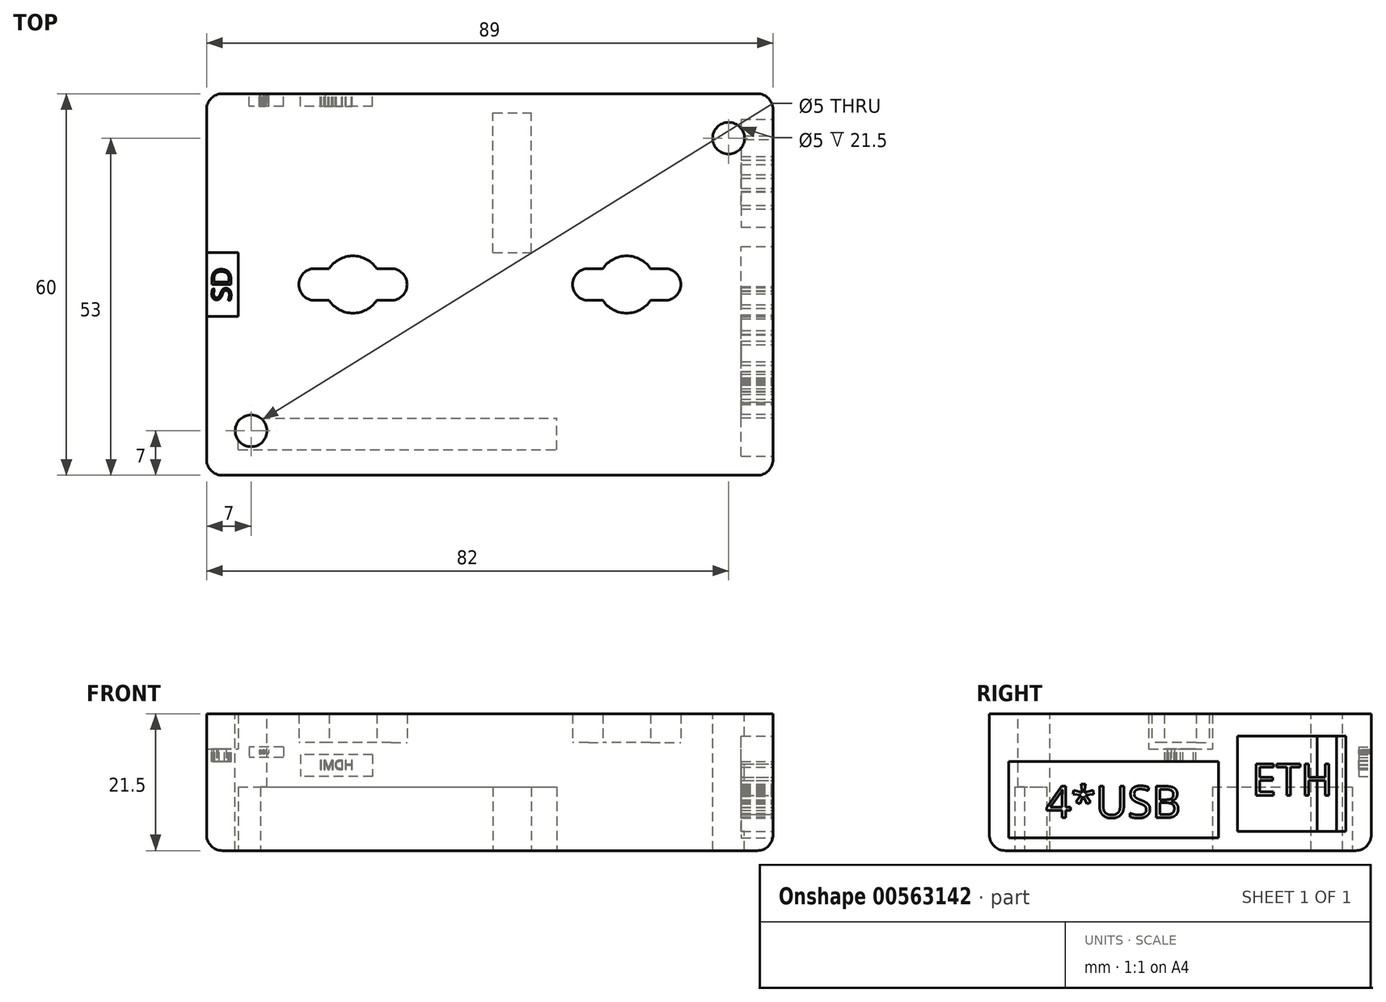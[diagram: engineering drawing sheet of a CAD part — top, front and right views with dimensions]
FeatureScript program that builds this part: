
annotation { "Feature Type Name" : "Feature", "Feature Type Description" : "" }
export const myFeature = defineFeature(function(context is Context, id is Id, definition is map)
    precondition{}
    {
        {
            var Q0;
            Q0=qCreatedBy(makeId("Top.planeOp"),FACE);
            var sketch = newSketch(context, id + "F0", { "sketchPlane" : qUnion([Q0])});
            skLineSegment(sketch, "E0.bottom", {"start": v(44.5, -30) * mm, "end": v(-44.5, -30) * mm});
            skLineSegment(sketch, "E0.top", {"start": v(44.5, 30) * mm, "end": v(-44.5, 30) * mm});
            skLineSegment(sketch, "E0.left", {"start": v(44.5, -30) * mm, "end": v(44.5, 30) * mm});
            skLineSegment(sketch, "E0.right", {"start": v(-44.5, -30) * mm, "end": v(-44.5, 30) * mm});
            skPoint(sketch, "E0.middle", {"position": v(0, 0) * mm});
            skLineSegment(sketch, "E1", {"start": v(-44.5, 0) * mm, "end": v(44.5, 0) * mm, "construction": true});
            skCircle(sketch, "E2", {"center": v(-37.5, 23) * mm, "radius": 2.5 * mm});
            skLineSegment(sketch, "E3", {"start": v(-37.5, 23) * mm, "end": v(-44.5, 23) * mm, "construction": true});
            skLineSegment(sketch, "E4", {"start": v(-44.5, 23) * mm, "end": v(-37.5, 23) * mm, "construction": true});
            skLineSegment(sketch, "E5", {"start": v(-37.5, 23) * mm, "end": v(-37.5, 30) * mm, "construction": true});
            skCircle(sketch, "E6", {"center": v(0, 0) * mm, "radius": 3.04 * mm, "construction": true});
            skCircle(sketch, "E7.MirrorC", {"center": v(-37.5, -23) * mm, "radius": 2.5 * mm});
            skLineSegment(sketch, "E8", {"start": v(0, 0) * mm, "end": v(0, 30) * mm, "construction": true});
            skCircle(sketch, "E9.MirrorC", {"center": v(37.5, 23) * mm, "radius": 2.5 * mm});
            skCircle(sketch, "E10.MirrorC", {"center": v(37.5, -23) * mm, "radius": 2.5 * mm});
            skArc(sketch, "E11", {"start": v(17.76, -2.5) * mm, "mid": v(21.5, -4.5) * mm, "end": v(25.24, -2.5) * mm});
            skArc(sketch, "E12", {"start": v(15.5, 2.5) * mm, "mid": v(13, 0) * mm, "end": v(15.5, -2.5) * mm});
            skLineSegment(sketch, "E13", {"start": v(15.5, 0) * mm, "end": v(21.5, 0) * mm, "construction": true});
            skLineSegment(sketch, "E14", {"start": v(21.5, 0) * mm, "end": v(44.5, 0) * mm, "construction": true});
            skLineSegment(sketch, "E15", {"start": v(21.5, 0) * mm, "end": v(21.5, 12.26) * mm, "construction": true});
            skArc(sketch, "E16.MirrorC", {"start": v(27.5, 2.5) * mm, "mid": v(30, 0) * mm, "end": v(27.5, -2.5) * mm});
            skLineSegment(sketch, "E17", {"start": v(15.5, 2.5) * mm, "end": v(17.76, 2.5) * mm});
            skLineSegment(sketch, "E18.MirrorCS", {"start": v(15.5, -2.5) * mm, "end": v(17.76, -2.5) * mm});
            skLineSegment(sketch, "E19.trimOffspring", {"start": v(25.24, 2.5) * mm, "end": v(27.5, 2.5) * mm});
            skArc(sketch, "E20.trimOffspring", {"start": v(25.24, 2.5) * mm, "mid": v(21.5, 4.5) * mm, "end": v(17.76, 2.5) * mm});
            skLineSegment(sketch, "E21.trimOffspring", {"start": v(25.24, -2.5) * mm, "end": v(27.5, -2.5) * mm});
            skLineSegment(sketch, "E22.MirrorCS", {"start": v(-15.5, -2.5) * mm, "end": v(-17.76, -2.5) * mm});
            skLineSegment(sketch, "E23.MirrorCS", {"start": v(-25.24, -2.5) * mm, "end": v(-27.5, -2.5) * mm});
            skLineSegment(sketch, "E24.MirrorCS", {"start": v(-25.24, 2.5) * mm, "end": v(-27.5, 2.5) * mm});
            skLineSegment(sketch, "E25.MirrorCS", {"start": v(-15.5, 2.5) * mm, "end": v(-17.76, 2.5) * mm});
            skArc(sketch, "E26.MirrorCS", {"start": v(-15.5, 2.5) * mm, "mid": v(-13, 0) * mm, "end": v(-15.5, -2.5) * mm});
            skArc(sketch, "E27.MirrorCS", {"start": v(-27.5, 2.5) * mm, "mid": v(-30, 0) * mm, "end": v(-27.5, -2.5) * mm});
            skLineSegment(sketch, "E28.MirrorCS", {"start": v(-15.5, 0) * mm, "end": v(-21.5, 0) * mm, "construction": true});
            skArc(sketch, "E29.MirrorCS", {"start": v(-25.24, 2.5) * mm, "mid": v(-21.5, 4.5) * mm, "end": v(-17.76, 2.5) * mm});
            skArc(sketch, "E30.MirrorCS", {"start": v(-17.76, -2.5) * mm, "mid": v(-21.5, -4.5) * mm, "end": v(-25.24, -2.5) * mm});
            skLineSegment(sketch, "E31.bottom", {"start": v(-44.5, -5) * mm, "end": v(-39.5, -5) * mm});
            skLineSegment(sketch, "E31.top", {"start": v(-44.5, 5) * mm, "end": v(-39.5, 5) * mm});
            skLineSegment(sketch, "E31.left", {"start": v(-44.5, -5) * mm, "end": v(-44.5, 5) * mm});
            skLineSegment(sketch, "E31.right", {"start": v(-39.5, -5) * mm, "end": v(-39.5, 5) * mm});
            skPoint(sketch, "E32", {"position": v(-39.5, 0) * mm});
            skSolve(sketch);
        }
        {
            var Q0;
            Q0=makeQuery(id+"F0.imprint","IMPRINT",FACE,{"disambiguationData":[TD([[makeQuery(id+"F0.imprint","IMPRINT",EDGE,{"derivedFrom":sQuery(id+"F0.wireOp",EDGE,"E0.bottom")}),-1.0]])]});
            var Q1;
            Q1=makeQuery(id+"F0.imprint","IMPRINT",FACE,{"disambiguationData":[TD([[makeQuery(id+"F0.imprint","IMPRINT",EDGE,{"derivedFrom":sQuery(id+"F0.wireOp",EDGE,"E7.MirrorC")}),-1.0]])]});
            var Q2;
            Q2=makeQuery(id+"F0.imprint","IMPRINT",FACE,{"disambiguationData":[TD([[makeQuery(id+"F0.imprint","IMPRINT",EDGE,{"derivedFrom":sQuery(id+"F0.wireOp",EDGE,"E10.MirrorC")}),1.0]])]});
            var Q3;
            Q3=makeQuery(id+"F0.imprint","IMPRINT",FACE,{"disambiguationData":[TD([[makeQuery(id+"F0.imprint","IMPRINT",EDGE,{"derivedFrom":sQuery(id+"F0.wireOp",EDGE,"E9.MirrorC")}),-1.0]])]});
            var Q4;
            Q4=makeQuery(id+"F0.imprint","IMPRINT",FACE,{"disambiguationData":[TD([[makeQuery(id+"F0.imprint","IMPRINT",EDGE,{"derivedFrom":sQuery(id+"F0.wireOp",EDGE,"E2")}),1.0]])]});
            var Q5;
            {var subQ0=sQuery(id+"F0.wireOp",EDGE,"E12");var subQ1=sQuery(id+"F0.wireOp",EDGE,"E11");var subQ2=makeQuery(id+"F0.imprint","INTERSECT",VERTEX,{"disambiguationData":[OD(0.0)],"derivedFrom":[subQ1,subQ0]});Q5=makeQuery(id+"F0.imprint","IMPRINT",FACE,{"disambiguationData":[TD([[makeQuery(id+"F0.imprint","IMPRINT",EDGE,{"disambiguationData":[TD([[subQ2,-1.0]])],"derivedFrom":subQ1}),-1.0]])]});}
            var Q6;
            {var subQ1=sQuery(id+"F0.wireOp",EDGE,"E11");var subQ5=sQuery(id+"F0.wireOp",EDGE,"E17");var subQ6=makeQuery(id+"F0.imprint","INTERSECT",VERTEX,{"disambiguationData":[OD(0.0)],"derivedFrom":[subQ1,subQ5]});Q6=makeQuery(id+"F0.imprint","IMPRINT",FACE,{"disambiguationData":[TD([[makeQuery(id+"F0.imprint","IMPRINT",EDGE,{"disambiguationData":[TD([[subQ6,1.0]])],"derivedFrom":subQ1}),1.0]])]});}
            var Q7;
            {var subQ0=sQuery(id+"F0.wireOp",EDGE,"E16.MirrorC");var subQ1=sQuery(id+"F0.wireOp",EDGE,"E11");var subQ2=makeQuery(id+"F0.imprint","INTERSECT",VERTEX,{"disambiguationData":[OD(0.0)],"derivedFrom":[subQ1,subQ0]});Q7=makeQuery(id+"F0.imprint","IMPRINT",FACE,{"disambiguationData":[TD([[makeQuery(id+"F0.imprint","IMPRINT",EDGE,{"disambiguationData":[TD([[subQ2,1.0]])],"derivedFrom":subQ1}),1.0]])]});}
            var Q8;
            {var subQ0=sQuery(id+"F0.wireOp",EDGE,"E16.MirrorC");var subQ1=sQuery(id+"F0.wireOp",EDGE,"E11");var subQ2=makeQuery(id+"F0.imprint","INTERSECT",VERTEX,{"disambiguationData":[OD(0.0)],"derivedFrom":[subQ1,subQ0]});Q8=makeQuery(id+"F0.imprint","IMPRINT",FACE,{"disambiguationData":[TD([[makeQuery(id+"F0.imprint","IMPRINT",EDGE,{"disambiguationData":[TD([[subQ2,1.0]])],"derivedFrom":subQ1}),-1.0]])]});}
            var Q9;
            {var subQ0=sQuery(id+"F0.wireOp",EDGE,"E18.MirrorCS");var subQ1=sQuery(id+"F0.wireOp",EDGE,"E11");var subQ2=makeQuery(id+"F0.imprint","INTERSECT",VERTEX,{"disambiguationData":[OD(1.0)],"derivedFrom":[subQ1,subQ0]});Q9=makeQuery(id+"F0.imprint","IMPRINT",FACE,{"disambiguationData":[TD([[makeQuery(id+"F0.imprint","IMPRINT",EDGE,{"disambiguationData":[TD([[subQ2,-1.0]])],"derivedFrom":subQ1}),-1.0]])]});}
            var Q10;
            {var subQ0=sQuery(id+"F0.wireOp",EDGE,"E12");var subQ1=sQuery(id+"F0.wireOp",EDGE,"E11");var subQ2=makeQuery(id+"F0.imprint","INTERSECT",VERTEX,{"disambiguationData":[OD(0.0)],"derivedFrom":[subQ1,subQ0]});Q10=makeQuery(id+"F0.imprint","IMPRINT",FACE,{"disambiguationData":[TD([[makeQuery(id+"F0.imprint","IMPRINT",EDGE,{"disambiguationData":[TD([[subQ2,-1.0]])],"derivedFrom":subQ1}),1.0]])]});}
            var Q11;
            Q11=makeQuery(id+"F0.imprint","IMPRINT",FACE,{"disambiguationData":[TD([[makeQuery(id+"F0.imprint","IMPRINT",EDGE,{"derivedFrom":sQuery(id+"F0.wireOp",EDGE,"E22.MirrorCS")}),-1.0]])]});
            var Q12;
            Q12=makeQuery(id+"F0.imprint","IMPRINT",FACE,{"disambiguationData":[TD([[makeQuery(id+"F0.imprint","IMPRINT",EDGE,{"derivedFrom":sQuery(id+"F0.wireOp",EDGE,"E31.bottom")}),1.0]])]});
            extrude(context, id + "F1", {"entities" : qUnion([Q0, Q1, Q2, Q3, Q4, Q5, Q6, Q7, Q8, Q9, Q10, Q11, Q12]), "oppositeDirection" : true, "depth" : 21 * mm, "offsetDistance" : 25 * mm});
        }
        {
            var Q0;
            Q0=makeQuery(id+"F0.imprint","IMPRINT",FACE,{"disambiguationData":[TD([[makeQuery(id+"F0.imprint","IMPRINT",EDGE,{"derivedFrom":sQuery(id+"F0.wireOp",EDGE,"E2")}),1.0]])]});
            var Q1;
            Q1=makeQuery(id+"F0.imprint","IMPRINT",FACE,{"disambiguationData":[TD([[makeQuery(id+"F0.imprint","IMPRINT",EDGE,{"derivedFrom":sQuery(id+"F0.wireOp",EDGE,"E7.MirrorC")}),-1.0]])]});
            var Q2;
            Q2=makeQuery(id+"F0.imprint","IMPRINT",FACE,{"disambiguationData":[TD([[makeQuery(id+"F0.imprint","IMPRINT",EDGE,{"derivedFrom":sQuery(id+"F0.wireOp",EDGE,"E10.MirrorC")}),1.0]])]});
            var Q3;
            Q3=makeQuery(id+"F0.imprint","IMPRINT",FACE,{"disambiguationData":[TD([[makeQuery(id+"F0.imprint","IMPRINT",EDGE,{"derivedFrom":sQuery(id+"F0.wireOp",EDGE,"E9.MirrorC")}),-1.0]])]});
            extrude(context, id + "F2", {"entities" : qUnion([Q0, Q1, Q2, Q3]), "operationType" : NewBodyOperationType.ADD, "depth" : 0.5 * mm, "offsetDistance" : 25 * mm});
        }
        {
            var Q0;
            Q0=makeQuery(id+"F0.imprint","IMPRINT",FACE,{"disambiguationData":[TD([[makeQuery(id+"F0.imprint","IMPRINT",EDGE,{"derivedFrom":sQuery(id+"F0.wireOp",EDGE,"E11")}),1.0]])]});
            var Q1;
            Q1=makeQuery(id+"F0.imprint","IMPRINT",FACE,{"disambiguationData":[TD([[makeQuery(id+"F0.imprint","IMPRINT",EDGE,{"derivedFrom":sQuery(id+"F0.wireOp",EDGE,"E22.MirrorCS")}),-1.0]])]});
            extrude(context, id + "F3", {"entities" : qUnion([Q0, Q1]), "operationType" : NewBodyOperationType.REMOVE, "oppositeDirection" : true, "depth" : 4 * mm, "offsetDistance" : 25 * mm});
        }
        {
            var Q0;
            Q0=makeQuery(id+"F1.opExtrude","SWEPT_FACE",FACE,{"disambiguationData":[OSD([sQuery(id+"F0.wireOp",EDGE,"E0.left")])]});
            var sketch = newSketch(context, id + "F4", { "sketchPlane" : qUnion([Q0])});
            skLineSegment(sketch, "E33.bottom", {"start": v(26, -18) * mm, "end": v(9, -18) * mm});
            skLineSegment(sketch, "E33.top", {"start": v(26, -3) * mm, "end": v(9, -3) * mm});
            skLineSegment(sketch, "E33.left", {"start": v(26, -18) * mm, "end": v(26, -3) * mm});
            skLineSegment(sketch, "E33.right", {"start": v(9, -18) * mm, "end": v(9, -3) * mm});
            skPoint(sketch, "E33.middle", {"position": v(17.5, -10.5) * mm});
            skLineSegment(sketch, "E34.bottom", {"start": v(-27, -7) * mm, "end": v(6, -7) * mm});
            skLineSegment(sketch, "E34.top", {"start": v(-27, -19) * mm, "end": v(6, -19) * mm});
            skLineSegment(sketch, "E34.left", {"start": v(-27, -7) * mm, "end": v(-27, -19) * mm});
            skLineSegment(sketch, "E34.right", {"start": v(6, -7) * mm, "end": v(6, -19) * mm});
            skLineSegment(sketch, "E35", {"start": v(1.06, -19) * mm, "end": v(1.06, -21) * mm, "construction": true});
            skLineSegment(sketch, "E36", {"start": v(-27, -13) * mm, "end": v(-30, -13) * mm, "construction": true});
            skText(sketch, "E37", { "text": "4*USB\n", "fontName": "OpenSans-Regular.ttf"});
            skLineSegment(sketch, "E38", {"start": v(23.65, -18) * mm, "end": v(23.65, -21) * mm, "construction": true});
            skLineSegment(sketch, "E39", {"start": v(26, -11.08) * mm, "end": v(30, -11.08) * mm, "construction": true});
            skText(sketch, "E40", { "text": "ETH", "fontName": "OpenSans-Regular.ttf"});
            skLineSegment(sketch, "E41", {"start": v(-10.5, -7) * mm, "end": v(-10.5, -19) * mm, "construction": true});
            skLineSegment(sketch, "E42", {"start": v(17.5, -3) * mm, "end": v(17.5, -18) * mm, "construction": true});
            const initialGuessF4  = {"E37": [-0.02112, -0.01583, 1, 0, 0.005], "E40": [0.0112, -0.0123, 1, 0, 0.005]};
            skSetInitialGuess(sketch, initialGuessF4);
            skSolve(sketch);
        }
        {
            var Q0;
            Q0 = qSketchRegion(id + "F4", true);
            var Q1;
            Q1=makeQuery(id+"F4.imprint","IMPRINT",FACE,{"disambiguationData":[TD([[makeQuery(id+"F4.imprint","IMPRINT",EDGE,{"derivedFrom":sQuery(id+"F4.wireOp",EDGE,"E37.sketch_text.stroke-82")}),1.0]])]});
            var Q2;
            Q2=makeQuery(id+"F4.imprint","IMPRINT",FACE,{"disambiguationData":[TD([[makeQuery(id+"F4.imprint","IMPRINT",EDGE,{"derivedFrom":sQuery(id+"F4.wireOp",EDGE,"E37.sketch_text.stroke-89")}),1.0]])]});
            var Q3;
            Q3=makeQuery(id+"F4.imprint","IMPRINT",FACE,{"disambiguationData":[TD([[makeQuery(id+"F4.imprint","IMPRINT",EDGE,{"derivedFrom":sQuery(id+"F4.wireOp",EDGE,"E37.sketch_text.stroke-11")}),1.0]])]});
            extrude(context, id + "F5", {"entities" : qUnion([Q0, Q1, Q2, Q3]), "operationType" : NewBodyOperationType.REMOVE, "oppositeDirection" : true, "depth" : 5 * mm, "offsetDistance" : 25 * mm});
        }
        {
            var Q0;
            Q0=makeQuery(id+"F0.imprint","IMPRINT",FACE,{"disambiguationData":[TD([[makeQuery(id+"F0.imprint","IMPRINT",EDGE,{"derivedFrom":sQuery(id+"F0.wireOp",EDGE,"E31.bottom")}),1.0]])]});
            extrude(context, id + "F6", {"entities" : qUnion([Q0]), "operationType" : NewBodyOperationType.REMOVE, "oppositeDirection" : true, "depth" : 5 * mm, "offsetDistance" : 25 * mm});
        }
        {
            var Q0;
            Q0=makeQuery(id+"F6.boolean.opBoolean","COPY",FACE,{"derivedFrom":makeQuery(id+"F6.opExtrude","CAP_FACE",FACE,{"disambiguationData":[OSD([sQuery(id+"F0.wireOp",EDGE,"E31.bottom"),sQuery(id+"F0.wireOp",EDGE,"E31.top"),sQuery(id+"F0.wireOp",EDGE,"E31.left"),sQuery(id+"F0.wireOp",EDGE,"E31.right")])],"isStart":false})});
            var sketch = newSketch(context, id + "F7", { "sketchPlane" : qUnion([Q0])});
            skText(sketch, "E43", { "text": "SD", "fontName": "OpenSans-Regular.ttf"});
            const initialGuessF7  = {"E43": [-0.04067, -0.00267, 0, 1, 0.003]};
            skSetInitialGuess(sketch, initialGuessF7);
            skSolve(sketch);
        }
        {
            var Q0;
            Q0 = qSketchRegion(id + "F7", true);
            extrude(context, id + "F8", {"entities" : qUnion([Q0]), "operationType" : NewBodyOperationType.REMOVE, "oppositeDirection" : true, "depth" : 2 * mm, "offsetDistance" : 25 * mm});
        }
        {
            var Q0;
            Q0=makeQuery(id+"F1.opExtrude","SWEPT_FACE",FACE,{"disambiguationData":[OSD([sQuery(id+"F0.wireOp",EDGE,"E0.top")])]});
            var sketch = newSketch(context, id + "F9", { "sketchPlane" : qUnion([Q0])});
            skLineSegment(sketch, "E44.bottom", {"start": v(32.4, -4.69) * mm, "end": v(37.83, -4.69) * mm});
            skLineSegment(sketch, "E44.top", {"start": v(32.4, -6.38) * mm, "end": v(37.83, -6.38) * mm});
            skLineSegment(sketch, "E44.left", {"start": v(32.4, -4.69) * mm, "end": v(32.4, -6.38) * mm});
            skLineSegment(sketch, "E44.right", {"start": v(37.83, -4.69) * mm, "end": v(37.83, -6.38) * mm});
            skLineSegment(sketch, "E45.bottom", {"start": v(18.42, -5.9) * mm, "end": v(29.74, -5.9) * mm});
            skLineSegment(sketch, "E45.top", {"start": v(18.42, -9.34) * mm, "end": v(29.74, -9.34) * mm});
            skLineSegment(sketch, "E45.left", {"start": v(18.42, -5.9) * mm, "end": v(18.42, -9.34) * mm});
            skLineSegment(sketch, "E45.right", {"start": v(29.74, -5.9) * mm, "end": v(29.74, -9.34) * mm});
            skText(sketch, "E46", { "text": "HDMI", "fontName": "OpenSans-Regular.ttf"});
            skText(sketch, "E47", { "text": "USB", "fontName": "OpenSans-Regular.ttf"});
            skLineSegment(sketch, "E48", {"start": v(24.08, -5.9) * mm, "end": v(24.08, -8.8) * mm, "construction": true});
            skLineSegment(sketch, "E49", {"start": v(35.48, -4.69) * mm, "end": v(35.48, -6.14) * mm, "construction": true});
            const initialGuessF9  = {"E46": [0.0214, -0.00825, 1, 0, 0.00148], "E47": [0.03464, -0.0058, 1, 0, 0.00062]};
            skSetInitialGuess(sketch, initialGuessF9);
            skSolve(sketch);
        }
        {
            var Q0;
            Q0=makeQuery(id+"F9.imprint","IMPRINT",FACE,{"disambiguationData":[TD([[makeQuery(id+"F9.imprint","IMPRINT",EDGE,{"derivedFrom":sQuery(id+"F9.wireOp",EDGE,"E44.bottom")}),-1.0]])]});
            var Q1;
            Q1=makeQuery(id+"F9.imprint","IMPRINT",FACE,{"disambiguationData":[TD([[makeQuery(id+"F9.imprint","IMPRINT",EDGE,{"derivedFrom":sQuery(id+"F9.wireOp",EDGE,"E45.bottom")}),-1.0]])]});
            var Q2;
            Q2=makeQuery(id+"F9.imprint","IMPRINT",FACE,{"disambiguationData":[TD([[makeQuery(id+"F9.imprint","IMPRINT",EDGE,{"derivedFrom":sQuery(id+"F9.wireOp",EDGE,"E46.sketch_text.stroke-19")}),1.0]])]});
            var Q3;
            Q3=makeQuery(id+"F9.imprint","IMPRINT",FACE,{"disambiguationData":[TD([[makeQuery(id+"F9.imprint","IMPRINT",EDGE,{"derivedFrom":sQuery(id+"F9.wireOp",EDGE,"E47.sketch_text.stroke-50")}),1.0]])]});
            var Q4;
            Q4=makeQuery(id+"F9.imprint","IMPRINT",FACE,{"disambiguationData":[TD([[makeQuery(id+"F9.imprint","IMPRINT",EDGE,{"derivedFrom":sQuery(id+"F9.wireOp",EDGE,"E47.sketch_text.stroke-57")}),1.0]])]});
            extrude(context, id + "F10", {"entities" : qUnion([Q0, Q1, Q2, Q3, Q4]), "operationType" : NewBodyOperationType.REMOVE, "oppositeDirection" : true, "depth" : 2 * mm, "offsetDistance" : 25 * mm});
        }
        {
            var Q0;
            Q0=makeQuery(id+"F1.opExtrude","CAP_FACE",FACE,{"disambiguationData":[OSD([sQuery(id+"F0.wireOp",EDGE,"E0.bottom"),sQuery(id+"F0.wireOp",EDGE,"E0.top"),sQuery(id+"F0.wireOp",EDGE,"E0.left"),sQuery(id+"F0.wireOp",EDGE,"E0.right"),sQuery(id+"F0.wireOp",EDGE,"E31.left")])],"isStart":false});
            var sketch = newSketch(context, id + "F11", { "sketchPlane" : qUnion([Q0])});
            skLineSegment(sketch, "E50.bottom", {"start": v(-39.5, 26) * mm, "end": v(10.5, 26) * mm});
            skLineSegment(sketch, "E50.top", {"start": v(-39.5, 21) * mm, "end": v(10.5, 21) * mm});
            skLineSegment(sketch, "E50.left", {"start": v(-39.5, 26) * mm, "end": v(-39.5, 21) * mm});
            skLineSegment(sketch, "E50.right", {"start": v(10.5, 26) * mm, "end": v(10.5, 21) * mm});
            skLineSegment(sketch, "E51.bottom", {"start": v(0.5, -5) * mm, "end": v(6.5, -5) * mm});
            skLineSegment(sketch, "E51.top", {"start": v(0.5, -27) * mm, "end": v(6.5, -27) * mm});
            skLineSegment(sketch, "E51.left", {"start": v(0.5, -5) * mm, "end": v(0.5, -27) * mm});
            skLineSegment(sketch, "E51.right", {"start": v(6.5, -5) * mm, "end": v(6.5, -27) * mm});
            skLineSegment(sketch, "E52", {"start": v(6.5, -11.28) * mm, "end": v(44.5, -11.28) * mm, "construction": true});
            skLineSegment(sketch, "E53", {"start": v(4.24, -27) * mm, "end": v(4.24, -30) * mm, "construction": true});
            skLineSegment(sketch, "E54", {"start": v(-39.5, 23.5) * mm, "end": v(-44.5, 23.5) * mm, "construction": true});
            skLineSegment(sketch, "E55", {"start": v(-36.3, 26) * mm, "end": v(-36.3, 30) * mm, "construction": true});
            skSolve(sketch);
        }
        {
            var Q0;
            Q0=makeQuery(id+"F11.imprint","IMPRINT",FACE,{"disambiguationData":[TD([[makeQuery(id+"F11.imprint","IMPRINT",EDGE,{"derivedFrom":sQuery(id+"F11.wireOp",EDGE,"E50.bottom")}),-1.0]])]});
            var Q1;
            Q1=makeQuery(id+"F11.imprint","IMPRINT",FACE,{"disambiguationData":[TD([[makeQuery(id+"F11.imprint","IMPRINT",EDGE,{"derivedFrom":sQuery(id+"F11.wireOp",EDGE,"E51.bottom")}),-1.0]])]});
            extrude(context, id + "F12", {"entities" : qUnion([Q0, Q1]), "operationType" : NewBodyOperationType.REMOVE, "oppositeDirection" : true, "depth" : 10 * mm, "offsetDistance" : 25 * mm});
        }
        {
            var Q0;
            Q0=makeQuery(id+"F1.opExtrude","CAP_EDGE",EDGE,{"disambiguationData":[OSD([sQuery(id+"F0.wireOp",EDGE,"E0.bottom")])],"isStart":false});
            var Q1;
            Q1=makeQuery(id+"F1.opExtrude","CAP_EDGE",EDGE,{"disambiguationData":[OSD([sQuery(id+"F0.wireOp",EDGE,"E0.right"),sQuery(id+"F0.wireOp",EDGE,"E31.left")])],"isStart":false});
            var Q2;
            Q2=makeQuery(id+"F1.opExtrude","CAP_EDGE",EDGE,{"disambiguationData":[OSD([sQuery(id+"F0.wireOp",EDGE,"E0.top")])],"isStart":false});
            var Q3;
            Q3=makeQuery(id+"F1.opExtrude","CAP_EDGE",EDGE,{"disambiguationData":[OSD([sQuery(id+"F0.wireOp",EDGE,"E0.left")])],"isStart":false});
            var Q4;
            Q4=makeQuery(id+"F1.opExtrude","SWEPT_EDGE",EDGE,{"disambiguationData":[OSD([sQuery(id+"F0.wireOp",EDGE,"E0.top"),sQuery(id+"F0.wireOp",EDGE,"E0.right")])]});
            var Q5;
            Q5=makeQuery(id+"F1.opExtrude","SWEPT_EDGE",EDGE,{"disambiguationData":[OSD([sQuery(id+"F0.wireOp",EDGE,"E0.top"),sQuery(id+"F0.wireOp",EDGE,"E0.left")])]});
            var Q6;
            Q6=makeQuery(id+"F1.opExtrude","SWEPT_EDGE",EDGE,{"disambiguationData":[OSD([sQuery(id+"F0.wireOp",EDGE,"E0.bottom"),sQuery(id+"F0.wireOp",EDGE,"E0.left")])]});
            var Q7;
            Q7=makeQuery(id+"F1.opExtrude","SWEPT_EDGE",EDGE,{"disambiguationData":[OSD([sQuery(id+"F0.wireOp",EDGE,"E0.bottom"),sQuery(id+"F0.wireOp",EDGE,"E0.right")])]});
            var Q8;
            Q8=makeQuery(id+"F1.opExtrude","CAP_EDGE",EDGE,{"disambiguationData":[OSD([sQuery(id+"F0.wireOp",EDGE,"E0.bottom")])],"isStart":true});
            var Q9;
            Q9=makeQuery(id+"F1.opExtrude","CAP_EDGE",EDGE,{"disambiguationData":[OSD([sQuery(id+"F0.wireOp",EDGE,"E0.left")])],"isStart":true});
            var Q10;
            Q10=makeQuery(id+"F1.opExtrude","CAP_EDGE",EDGE,{"disambiguationData":[OSD([sQuery(id+"F0.wireOp",EDGE,"E0.top")])],"isStart":true});
            var Q11;
            {var subQ0=sQuery(id+"F0.wireOp",EDGE,"E31.left");var subQ1=sQuery(id+"F0.wireOp",EDGE,"E0.right");var subQ2=sQuery(id+"F0.wireOp",EDGE,"E0.top");Q11=makeQuery(id+"F6.boolean.opBoolean","SPLIT",EDGE,{"disambiguationData":[TD([makeQuery(id+"F1.opExtrude","SWEPT_FACE",FACE,{"disambiguationData":[OSD([subQ2])]})])],"derivedFrom":makeQuery(id+"F1.opExtrude","CAP_EDGE",EDGE,{"disambiguationData":[OSD([subQ1,subQ0])],"isStart":true})});}
            var Q12;
            {var subQ0=sQuery(id+"F0.wireOp",EDGE,"E0.bottom");var subQ1=sQuery(id+"F0.wireOp",EDGE,"E31.left");var subQ2=sQuery(id+"F0.wireOp",EDGE,"E0.right");Q12=makeQuery(id+"F6.boolean.opBoolean","SPLIT",EDGE,{"disambiguationData":[TD([makeQuery(id+"F1.opExtrude","SWEPT_FACE",FACE,{"disambiguationData":[OSD([subQ0])]})])],"derivedFrom":makeQuery(id+"F1.opExtrude","CAP_EDGE",EDGE,{"disambiguationData":[OSD([subQ2,subQ1])],"isStart":true})});}
            fillet(context, id + "F13", {"entities" : qUnion([Q0, Q1, Q2, Q3, Q4, Q5, Q6, Q7, Q8, Q9, Q10, Q11, Q12]), "radius" : 2.5 * mm, "tangentPropagation" : true, "allowEdgeOverflow" : false});
        }
    });
